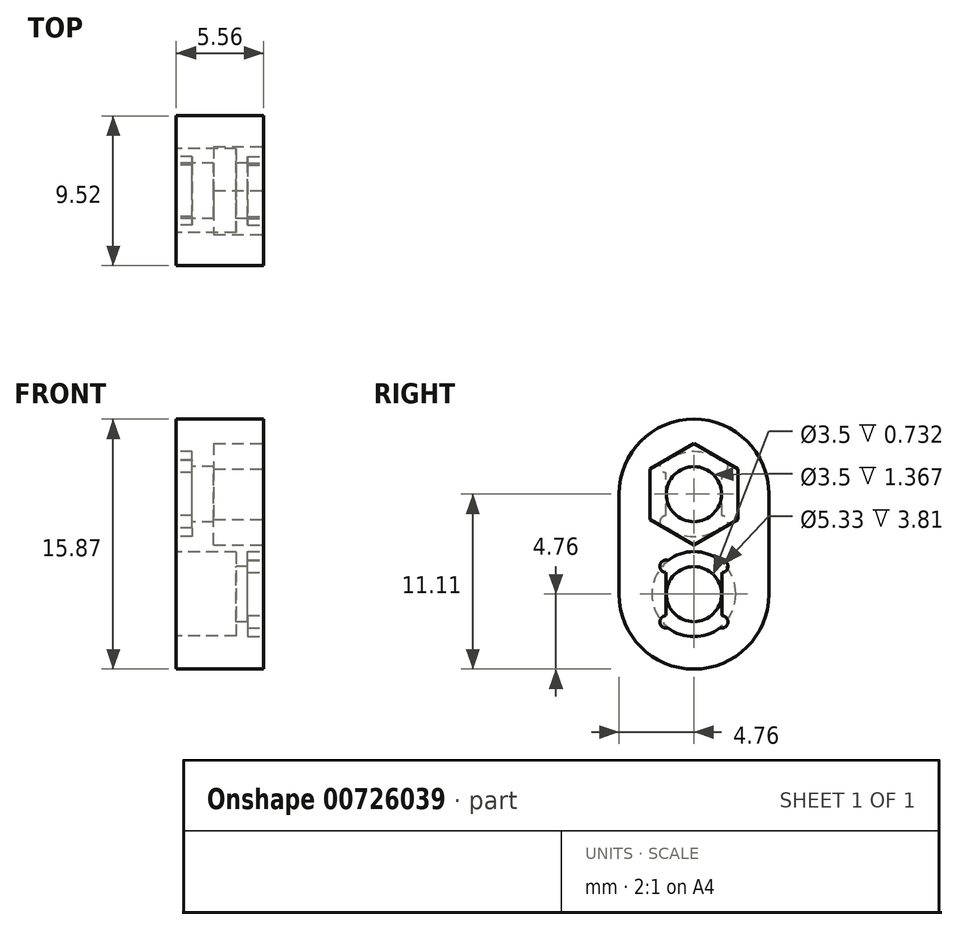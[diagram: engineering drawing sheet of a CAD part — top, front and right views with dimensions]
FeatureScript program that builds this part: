
annotation { "Feature Type Name" : "Feature", "Feature Type Description" : "" }
export const myFeature = defineFeature(function(context is Context, id is Id, definition is map)
    precondition{}
    {
        {
            var Q0;
            Q0=qCreatedBy(makeId("Right.planeOp"),FACE);
            var sketch = newSketch(context, id + "F0", { "sketchPlane" : qUnion([Q0])});
            skCircle(sketch, "E0", {"center": v(0, 0) * mm, "radius": 4.76 * mm});
            skCircle(sketch, "E1", {"center": v(0, 0) * mm, "radius": 1.75 * mm});
            skCircle(sketch, "E2", {"center": v(0, -6.35) * mm, "radius": 4.76 * mm});
            skCircle(sketch, "E3", {"center": v(0, -6.35) * mm, "radius": 1.75 * mm});
            skLineSegment(sketch, "E4", {"start": v(-4.76, 0) * mm, "end": v(-4.76, -6.35) * mm});
            skLineSegment(sketch, "E5", {"start": v(4.76, 0) * mm, "end": v(4.76, -6.35) * mm});
            skSolve(sketch);
        }
        {
            var Q0;
            Q0=makeQuery(id+"F0.imprint","IMPRINT",FACE,{"disambiguationData":[TD([[makeQuery(id+"F0.imprint","IMPRINT",EDGE,{"derivedFrom":sQuery(id+"F0.wireOp",EDGE,"E1")}),-1.0]])]});
            var Q1;
            {var subQ0=sQuery(id+"F0.wireOp",EDGE,"E5");Q1=makeQuery(id+"F0.imprint","IMPRINT",FACE,{"disambiguationData":[TD([[makeQuery(id+"F0.imprint","IMPRINT",EDGE,{"derivedFrom":subQ0}),-1.0]])]});}
            var Q2;
            {var subQ0=sQuery(id+"F0.wireOp",EDGE,"E2");var subQ1=sQuery(id+"F0.wireOp",EDGE,"E0");var subQ2=makeQuery(id+"F0.imprint","INTERSECT",VERTEX,{"disambiguationData":[OD(0.0)],"derivedFrom":[subQ1,subQ0]});Q2=makeQuery(id+"F0.imprint","IMPRINT",FACE,{"disambiguationData":[TD([[makeQuery(id+"F0.imprint","IMPRINT",EDGE,{"disambiguationData":[TD([[subQ2,-1.0]])],"derivedFrom":subQ1}),1.0]])]});}
            var Q3;
            Q3=makeQuery(id+"F0.imprint","IMPRINT",FACE,{"disambiguationData":[TD([[makeQuery(id+"F0.imprint","IMPRINT",EDGE,{"derivedFrom":sQuery(id+"F0.wireOp",EDGE,"E3")}),-1.0]])]});
            var Q4;
            {var subQ0=sQuery(id+"F0.wireOp",EDGE,"E4");Q4=makeQuery(id+"F0.imprint","IMPRINT",FACE,{"disambiguationData":[TD([[makeQuery(id+"F0.imprint","IMPRINT",EDGE,{"derivedFrom":subQ0}),1.0]])]});}
            extrude(context, id + "F1", {"entities" : qUnion([Q0, Q1, Q2, Q3, Q4]), "depth" : 5.56 * mm, "offsetDistance" : 25.4 * mm});
        }
        {
            var Q0;
            Q0=makeQuery(id+"F1.opExtrude","CAP_FACE",FACE,{"disambiguationData":[OSD([sQuery(id+"F0.wireOp",EDGE,"E0"),sQuery(id+"F0.wireOp",EDGE,"E1"),sQuery(id+"F0.wireOp",EDGE,"E2"),sQuery(id+"F0.wireOp",EDGE,"E3"),sQuery(id+"F0.wireOp",EDGE,"E4"),sQuery(id+"F0.wireOp",EDGE,"E5")])],"isStart":false});
            var sketch = newSketch(context, id + "F2", { "sketchPlane" : qUnion([Q0])});
            skLineSegment(sketch, "E6.bottom", {"start": v(-1.77, -8.12) * mm, "end": v(1.77, -8.12) * mm});
            skLineSegment(sketch, "E6.top", {"start": v(-1.77, -4.58) * mm, "end": v(1.77, -4.58) * mm});
            skLineSegment(sketch, "E6.left", {"start": v(-1.77, -8.12) * mm, "end": v(-1.77, -4.58) * mm});
            skLineSegment(sketch, "E6.right", {"start": v(1.77, -8.12) * mm, "end": v(1.77, -4.58) * mm});
            skPoint(sketch, "E6.middle", {"position": v(0, -6.35) * mm});
            skCircle(sketch, "E7", {"center": v(1.77, -4.58) * mm, "radius": 0.4 * mm});
            skCircle(sketch, "E8", {"center": v(-1.77, -4.58) * mm, "radius": 0.4 * mm});
            skCircle(sketch, "E9", {"center": v(-1.77, -8.12) * mm, "radius": 0.4 * mm});
            skCircle(sketch, "E10", {"center": v(1.77, -8.12) * mm, "radius": 0.4 * mm});
            skCircle(sketch, "E11.cCircle", {"center": v(0, 0) * mm, "radius": 3.23 * mm, "construction": true});
            skLineSegment(sketch, "E11.0", {"start": v(0, -3.23) * mm, "end": v(-2.8, -1.61) * mm});
            skLineSegment(sketch, "E11.1", {"start": v(-2.8, -1.61) * mm, "end": v(-2.8, 1.61) * mm});
            skLineSegment(sketch, "E11.2", {"start": v(-2.8, 1.61) * mm, "end": v(0, 3.23) * mm});
            skLineSegment(sketch, "E11.3", {"start": v(0, 3.23) * mm, "end": v(2.8, 1.61) * mm});
            skLineSegment(sketch, "E11.4", {"start": v(2.8, 1.61) * mm, "end": v(2.8, -1.61) * mm});
            skLineSegment(sketch, "E11.5", {"start": v(2.8, -1.61) * mm, "end": v(0, -3.23) * mm});
            skCircle(sketch, "E12", {"center": v(0, -6.35) * mm, "radius": 2.7 * mm});
            skSolve(sketch);
        }
        {
            var Q0;
            {var subQ0=sQuery(id+"F2.wireOp",EDGE,"E6.right");var subQ1=sQuery(id+"F2.wireOp",EDGE,"E6.top");var subQ2=makeQuery(id+"F2.imprint","INTERSECT",VERTEX,{"derivedFrom":[subQ1,subQ0]});Q0=makeQuery(id+"F2.imprint","IMPRINT",FACE,{"disambiguationData":[TD([[makeQuery(id+"F2.imprint","IMPRINT",EDGE,{"disambiguationData":[TD([[subQ2,1.0]])],"derivedFrom":subQ1}),-1.0]])]});}
            var Q1;
            {var subQ0=sQuery(id+"F2.wireOp",EDGE,"E6.right");var subQ1=sQuery(id+"F2.wireOp",EDGE,"E6.top");var subQ2=makeQuery(id+"F2.imprint","INTERSECT",VERTEX,{"derivedFrom":[subQ1,subQ0]});Q1=makeQuery(id+"F2.imprint","IMPRINT",FACE,{"disambiguationData":[TD([[makeQuery(id+"F2.imprint","IMPRINT",EDGE,{"disambiguationData":[TD([[subQ2,1.0]])],"derivedFrom":subQ1}),1.0]])]});}
            var Q2;
            {var subQ0=sQuery(id+"F2.wireOp",EDGE,"E6.right");var subQ1=sQuery(id+"F2.wireOp",EDGE,"E6.bottom");var subQ2=makeQuery(id+"F2.imprint","INTERSECT",VERTEX,{"derivedFrom":[subQ1,subQ0]});Q2=makeQuery(id+"F2.imprint","IMPRINT",FACE,{"disambiguationData":[TD([[makeQuery(id+"F2.imprint","IMPRINT",EDGE,{"disambiguationData":[TD([[subQ2,1.0]])],"derivedFrom":subQ1}),1.0]])]});}
            var Q3;
            {var subQ0=sQuery(id+"F2.wireOp",EDGE,"E6.right");var subQ1=sQuery(id+"F2.wireOp",EDGE,"E6.bottom");var subQ2=makeQuery(id+"F2.imprint","INTERSECT",VERTEX,{"derivedFrom":[subQ1,subQ0]});Q3=makeQuery(id+"F2.imprint","IMPRINT",FACE,{"disambiguationData":[TD([[makeQuery(id+"F2.imprint","IMPRINT",EDGE,{"disambiguationData":[TD([[subQ2,1.0]])],"derivedFrom":subQ1}),-1.0]])]});}
            var Q4;
            {var subQ0=sQuery(id+"F2.wireOp",EDGE,"E6.left");var subQ1=sQuery(id+"F2.wireOp",EDGE,"E6.bottom");var subQ2=makeQuery(id+"F2.imprint","INTERSECT",VERTEX,{"derivedFrom":[subQ1,subQ0]});Q4=makeQuery(id+"F2.imprint","IMPRINT",FACE,{"disambiguationData":[TD([[makeQuery(id+"F2.imprint","IMPRINT",EDGE,{"disambiguationData":[TD([[subQ2,-1.0]])],"derivedFrom":subQ1}),-1.0]])]});}
            var Q5;
            {var subQ0=sQuery(id+"F2.wireOp",EDGE,"E6.left");var subQ1=sQuery(id+"F2.wireOp",EDGE,"E6.bottom");var subQ2=makeQuery(id+"F2.imprint","INTERSECT",VERTEX,{"derivedFrom":[subQ1,subQ0]});Q5=makeQuery(id+"F2.imprint","IMPRINT",FACE,{"disambiguationData":[TD([[makeQuery(id+"F2.imprint","IMPRINT",EDGE,{"disambiguationData":[TD([[subQ2,-1.0]])],"derivedFrom":subQ1}),1.0]])]});}
            var Q6;
            {var subQ0=sQuery(id+"F2.wireOp",EDGE,"E6.left");var subQ1=sQuery(id+"F2.wireOp",EDGE,"E6.top");var subQ2=makeQuery(id+"F2.imprint","INTERSECT",VERTEX,{"derivedFrom":[subQ1,subQ0]});Q6=makeQuery(id+"F2.imprint","IMPRINT",FACE,{"disambiguationData":[TD([[makeQuery(id+"F2.imprint","IMPRINT",EDGE,{"disambiguationData":[TD([[subQ2,-1.0]])],"derivedFrom":subQ1}),-1.0]])]});}
            var Q7;
            {var subQ0=sQuery(id+"F2.wireOp",EDGE,"E6.left");var subQ1=sQuery(id+"F2.wireOp",EDGE,"E6.top");var subQ2=makeQuery(id+"F2.imprint","INTERSECT",VERTEX,{"derivedFrom":[subQ1,subQ0]});Q7=makeQuery(id+"F2.imprint","IMPRINT",FACE,{"disambiguationData":[TD([[makeQuery(id+"F2.imprint","IMPRINT",EDGE,{"disambiguationData":[TD([[subQ2,-1.0]])],"derivedFrom":subQ1}),1.0]])]});}
            var Q8;
            {var subQ1=sQuery(id+"F2.wireOp",EDGE,"E6.top");var subQ7=sQuery(id+"F2.wireOp",EDGE,"E8");var subQ11=makeQuery(id+"F2.imprint","INTERSECT",VERTEX,{"derivedFrom":[subQ1,subQ7]});Q8=makeQuery(id+"F2.imprint","IMPRINT",FACE,{"disambiguationData":[TD([[makeQuery(id+"F2.imprint","IMPRINT",EDGE,{"disambiguationData":[TD([[subQ11,-1.0]])],"derivedFrom":subQ1}),-1.0]])]});}
            var Q9;
            {var subQ0=sQuery(id+"F2.wireOp",EDGE,"E9");var subQ1=sQuery(id+"F2.wireOp",EDGE,"E6.bottom");var subQ2=makeQuery(id+"F2.imprint","INTERSECT",VERTEX,{"derivedFrom":[subQ1,subQ0]});Q9=makeQuery(id+"F2.imprint","IMPRINT",FACE,{"disambiguationData":[TD([[makeQuery(id+"F2.imprint","IMPRINT",EDGE,{"disambiguationData":[TD([[subQ2,-1.0]])],"derivedFrom":subQ1}),1.0]])]});}
            var Q10;
            {var subQ0=sQuery(id+"F2.wireOp",EDGE,"E12");var subQ1=sQuery(id+"F2.wireOp",EDGE,"E6.top");var subQ10=makeQuery(id+"F2.imprint","INTERSECT",VERTEX,{"disambiguationData":[OD(0.0)],"derivedFrom":[subQ1,subQ0]});Q10=makeQuery(id+"F2.imprint","IMPRINT",FACE,{"disambiguationData":[TD([[makeQuery(id+"F2.imprint","IMPRINT",EDGE,{"disambiguationData":[TD([[subQ10,-1.0]])],"derivedFrom":subQ1}),-1.0]])]});}
            var Q11;
            {var subQ0=sQuery(id+"F2.wireOp",EDGE,"E12");var subQ1=sQuery(id+"F2.wireOp",EDGE,"E6.top");var subQ2=makeQuery(id+"F2.imprint","INTERSECT",VERTEX,{"disambiguationData":[OD(1.0)],"derivedFrom":[subQ1,subQ0]});Q11=makeQuery(id+"F2.imprint","IMPRINT",FACE,{"disambiguationData":[TD([[makeQuery(id+"F2.imprint","IMPRINT",EDGE,{"disambiguationData":[TD([[subQ2,-1.0]])],"derivedFrom":subQ1}),-1.0]])]});}
            var Q12;
            {var subQ0=sQuery(id+"F2.wireOp",EDGE,"E12");var subQ1=sQuery(id+"F2.wireOp",EDGE,"E6.top");var subQ2=makeQuery(id+"F2.imprint","INTERSECT",VERTEX,{"disambiguationData":[OD(0.0)],"derivedFrom":[subQ1,subQ0]});Q12=makeQuery(id+"F2.imprint","IMPRINT",FACE,{"disambiguationData":[TD([[makeQuery(id+"F2.imprint","IMPRINT",EDGE,{"disambiguationData":[TD([[subQ2,-1.0]])],"derivedFrom":subQ1}),1.0]])]});}
            var Q13;
            {var subQ0=sQuery(id+"F2.wireOp",EDGE,"E12");var subQ7=sQuery(id+"F2.wireOp",EDGE,"E6.bottom");var subQ8=makeQuery(id+"F2.imprint","INTERSECT",VERTEX,{"disambiguationData":[OD(0.0)],"derivedFrom":[subQ7,subQ0]});Q13=makeQuery(id+"F2.imprint","IMPRINT",FACE,{"disambiguationData":[TD([[makeQuery(id+"F2.imprint","IMPRINT",EDGE,{"disambiguationData":[TD([[subQ8,-1.0]])],"derivedFrom":subQ7}),1.0]])]});}
            var Q14;
            {var subQ0=sQuery(id+"F2.wireOp",EDGE,"E12");var subQ1=sQuery(id+"F2.wireOp",EDGE,"E6.bottom");var subQ2=makeQuery(id+"F2.imprint","INTERSECT",VERTEX,{"disambiguationData":[OD(1.0)],"derivedFrom":[subQ1,subQ0]});Q14=makeQuery(id+"F2.imprint","IMPRINT",FACE,{"disambiguationData":[TD([[makeQuery(id+"F2.imprint","IMPRINT",EDGE,{"disambiguationData":[TD([[subQ2,-1.0]])],"derivedFrom":subQ1}),1.0]])]});}
            var Q15;
            {var subQ0=sQuery(id+"F2.wireOp",EDGE,"E12");var subQ1=sQuery(id+"F2.wireOp",EDGE,"E6.bottom");var subQ2=makeQuery(id+"F2.imprint","INTERSECT",VERTEX,{"disambiguationData":[OD(0.0)],"derivedFrom":[subQ1,subQ0]});Q15=makeQuery(id+"F2.imprint","IMPRINT",FACE,{"disambiguationData":[TD([[makeQuery(id+"F2.imprint","IMPRINT",EDGE,{"disambiguationData":[TD([[subQ2,-1.0]])],"derivedFrom":subQ1}),-1.0]])]});}
            var Q16;
            {var subQ0=sQuery(id+"F2.wireOp",EDGE,"E12");var subQ1=sQuery(id+"F2.wireOp",EDGE,"E8");var subQ2=makeQuery(id+"F2.imprint","INTERSECT",VERTEX,{"disambiguationData":[OD(0.0)],"derivedFrom":[subQ1,subQ0]});Q16=makeQuery(id+"F2.imprint","IMPRINT",FACE,{"disambiguationData":[TD([[makeQuery(id+"F2.imprint","IMPRINT",EDGE,{"disambiguationData":[TD([[subQ2,-1.0]])],"derivedFrom":subQ1}),1.0]])]});}
            var Q17;
            {var subQ0=sQuery(id+"F2.wireOp",EDGE,"E12");var subQ1=sQuery(id+"F2.wireOp",EDGE,"E7");var subQ2=makeQuery(id+"F2.imprint","INTERSECT",VERTEX,{"disambiguationData":[OD(0.0)],"derivedFrom":[subQ1,subQ0]});Q17=makeQuery(id+"F2.imprint","IMPRINT",FACE,{"disambiguationData":[TD([[makeQuery(id+"F2.imprint","IMPRINT",EDGE,{"disambiguationData":[TD([[subQ2,1.0]])],"derivedFrom":subQ1}),1.0]])]});}
            var Q18;
            {var subQ0=sQuery(id+"F2.wireOp",EDGE,"E12");var subQ1=sQuery(id+"F2.wireOp",EDGE,"E10");var subQ2=makeQuery(id+"F2.imprint","INTERSECT",VERTEX,{"disambiguationData":[OD(0.0)],"derivedFrom":[subQ1,subQ0]});Q18=makeQuery(id+"F2.imprint","IMPRINT",FACE,{"disambiguationData":[TD([[makeQuery(id+"F2.imprint","IMPRINT",EDGE,{"disambiguationData":[TD([[subQ2,1.0]])],"derivedFrom":subQ1}),1.0]])]});}
            var Q19;
            {var subQ0=sQuery(id+"F2.wireOp",EDGE,"E12");var subQ1=sQuery(id+"F2.wireOp",EDGE,"E9");var subQ2=makeQuery(id+"F2.imprint","INTERSECT",VERTEX,{"disambiguationData":[OD(0.0)],"derivedFrom":[subQ1,subQ0]});Q19=makeQuery(id+"F2.imprint","IMPRINT",FACE,{"disambiguationData":[TD([[makeQuery(id+"F2.imprint","IMPRINT",EDGE,{"disambiguationData":[TD([[subQ2,-1.0]])],"derivedFrom":subQ1}),1.0]])]});}
            var Q20;
            {var subQ0=sQuery(id+"F2.wireOp",EDGE,"E8");var subQ1=sQuery(id+"F2.wireOp",EDGE,"E6.top");var subQ2=makeQuery(id+"F2.imprint","INTERSECT",VERTEX,{"derivedFrom":[subQ1,subQ0]});Q20=makeQuery(id+"F2.imprint","IMPRINT",FACE,{"disambiguationData":[TD([[makeQuery(id+"F2.imprint","IMPRINT",EDGE,{"disambiguationData":[TD([[subQ2,-1.0]])],"derivedFrom":subQ1}),1.0]])]});}
            var Q21;
            {var subQ0=sQuery(id+"F2.wireOp",EDGE,"E9");var subQ1=sQuery(id+"F2.wireOp",EDGE,"E6.bottom");var subQ2=makeQuery(id+"F2.imprint","INTERSECT",VERTEX,{"derivedFrom":[subQ1,subQ0]});Q21=makeQuery(id+"F2.imprint","IMPRINT",FACE,{"disambiguationData":[TD([[makeQuery(id+"F2.imprint","IMPRINT",EDGE,{"disambiguationData":[TD([[subQ2,-1.0]])],"derivedFrom":subQ1}),-1.0]])]});}
            extrude(context, id + "F3", {"entities" : qUnion([Q0, Q1, Q2, Q3, Q4, Q5, Q6, Q7, Q8, Q9, Q10, Q11, Q12, Q13, Q14, Q15, Q16, Q17, Q18, Q19, Q20, Q21]), "operationType" : NewBodyOperationType.REMOVE, "oppositeDirection" : true, "depth" : 1.02 * mm, "offsetDistance" : 25.4 * mm});
        }
        {
            var Q0;
            Q0=makeQuery(id+"F1.opExtrude","CAP_FACE",FACE,{"disambiguationData":[OSD([sQuery(id+"F0.wireOp",EDGE,"E0"),sQuery(id+"F0.wireOp",EDGE,"E1"),sQuery(id+"F0.wireOp",EDGE,"E2"),sQuery(id+"F0.wireOp",EDGE,"E3"),sQuery(id+"F0.wireOp",EDGE,"E4"),sQuery(id+"F0.wireOp",EDGE,"E5")])],"isStart":true});
            var sketch = newSketch(context, id + "F4", { "sketchPlane" : qUnion([Q0])});
            skLineSegment(sketch, "E13.bottom", {"start": v(-1.77, -1.77) * mm, "end": v(1.77, -1.77) * mm});
            skLineSegment(sketch, "E13.top", {"start": v(-1.77, 1.77) * mm, "end": v(1.77, 1.77) * mm});
            skLineSegment(sketch, "E13.left", {"start": v(-1.77, -1.77) * mm, "end": v(-1.77, 1.77) * mm});
            skLineSegment(sketch, "E13.right", {"start": v(1.77, -1.77) * mm, "end": v(1.77, 1.77) * mm});
            skPoint(sketch, "E13.middle", {"position": v(0, 0) * mm});
            skCircle(sketch, "E14", {"center": v(1.77, 1.77) * mm, "radius": 0.4 * mm});
            skCircle(sketch, "E15", {"center": v(-1.77, 1.77) * mm, "radius": 0.4 * mm});
            skCircle(sketch, "E16", {"center": v(-1.77, -1.77) * mm, "radius": 0.4 * mm});
            skCircle(sketch, "E17", {"center": v(1.77, -1.77) * mm, "radius": 0.4 * mm});
            skCircle(sketch, "E18.cCircle", {"center": v(0, -6.35) * mm, "radius": 3.23 * mm, "construction": true});
            skLineSegment(sketch, "E18.0", {"start": v(0, -9.58) * mm, "end": v(-2.8, -7.96) * mm});
            skLineSegment(sketch, "E18.1", {"start": v(-2.8, -7.96) * mm, "end": v(-2.8, -4.74) * mm});
            skLineSegment(sketch, "E18.2", {"start": v(-2.8, -4.74) * mm, "end": v(0, -3.12) * mm});
            skLineSegment(sketch, "E18.3", {"start": v(0, -3.12) * mm, "end": v(2.8, -4.74) * mm});
            skLineSegment(sketch, "E18.4", {"start": v(2.8, -4.74) * mm, "end": v(2.8, -7.96) * mm});
            skLineSegment(sketch, "E18.5", {"start": v(2.8, -7.96) * mm, "end": v(0, -9.58) * mm});
            skCircle(sketch, "E19", {"center": v(0, 0) * mm, "radius": 2.7 * mm});
            skSolve(sketch);
        }
        {
            var Q0;
            {var subQ0=sQuery(id+"F4.wireOp",EDGE,"E13.right");var subQ1=sQuery(id+"F4.wireOp",EDGE,"E13.bottom");var subQ2=makeQuery(id+"F4.imprint","INTERSECT",VERTEX,{"derivedFrom":[subQ1,subQ0]});Q0=makeQuery(id+"F4.imprint","IMPRINT",FACE,{"disambiguationData":[TD([[makeQuery(id+"F4.imprint","IMPRINT",EDGE,{"disambiguationData":[TD([[subQ2,1.0]])],"derivedFrom":subQ1}),1.0]])]});}
            var Q1;
            {var subQ0=sQuery(id+"F4.wireOp",EDGE,"E13.right");var subQ1=sQuery(id+"F4.wireOp",EDGE,"E13.bottom");var subQ2=makeQuery(id+"F4.imprint","INTERSECT",VERTEX,{"derivedFrom":[subQ1,subQ0]});Q1=makeQuery(id+"F4.imprint","IMPRINT",FACE,{"disambiguationData":[TD([[makeQuery(id+"F4.imprint","IMPRINT",EDGE,{"disambiguationData":[TD([[subQ2,1.0]])],"derivedFrom":subQ1}),-1.0]])]});}
            var Q2;
            {var subQ0=sQuery(id+"F4.wireOp",EDGE,"E13.left");var subQ1=sQuery(id+"F4.wireOp",EDGE,"E13.bottom");var subQ2=makeQuery(id+"F4.imprint","INTERSECT",VERTEX,{"derivedFrom":[subQ1,subQ0]});Q2=makeQuery(id+"F4.imprint","IMPRINT",FACE,{"disambiguationData":[TD([[makeQuery(id+"F4.imprint","IMPRINT",EDGE,{"disambiguationData":[TD([[subQ2,-1.0]])],"derivedFrom":subQ1}),1.0]])]});}
            var Q3;
            {var subQ0=sQuery(id+"F4.wireOp",EDGE,"E13.left");var subQ1=sQuery(id+"F4.wireOp",EDGE,"E13.bottom");var subQ2=makeQuery(id+"F4.imprint","INTERSECT",VERTEX,{"derivedFrom":[subQ1,subQ0]});Q3=makeQuery(id+"F4.imprint","IMPRINT",FACE,{"disambiguationData":[TD([[makeQuery(id+"F4.imprint","IMPRINT",EDGE,{"disambiguationData":[TD([[subQ2,-1.0]])],"derivedFrom":subQ1}),-1.0]])]});}
            var Q4;
            {var subQ0=sQuery(id+"F4.wireOp",EDGE,"E13.left");var subQ1=sQuery(id+"F4.wireOp",EDGE,"E13.top");var subQ2=makeQuery(id+"F4.imprint","INTERSECT",VERTEX,{"derivedFrom":[subQ1,subQ0]});Q4=makeQuery(id+"F4.imprint","IMPRINT",FACE,{"disambiguationData":[TD([[makeQuery(id+"F4.imprint","IMPRINT",EDGE,{"disambiguationData":[TD([[subQ2,-1.0]])],"derivedFrom":subQ1}),-1.0]])]});}
            var Q5;
            {var subQ0=sQuery(id+"F4.wireOp",EDGE,"E13.left");var subQ1=sQuery(id+"F4.wireOp",EDGE,"E13.top");var subQ2=makeQuery(id+"F4.imprint","INTERSECT",VERTEX,{"derivedFrom":[subQ1,subQ0]});Q5=makeQuery(id+"F4.imprint","IMPRINT",FACE,{"disambiguationData":[TD([[makeQuery(id+"F4.imprint","IMPRINT",EDGE,{"disambiguationData":[TD([[subQ2,-1.0]])],"derivedFrom":subQ1}),1.0]])]});}
            var Q6;
            {var subQ0=sQuery(id+"F4.wireOp",EDGE,"E13.right");var subQ1=sQuery(id+"F4.wireOp",EDGE,"E13.top");var subQ2=makeQuery(id+"F4.imprint","INTERSECT",VERTEX,{"derivedFrom":[subQ1,subQ0]});Q6=makeQuery(id+"F4.imprint","IMPRINT",FACE,{"disambiguationData":[TD([[makeQuery(id+"F4.imprint","IMPRINT",EDGE,{"disambiguationData":[TD([[subQ2,1.0]])],"derivedFrom":subQ1}),-1.0]])]});}
            var Q7;
            {var subQ0=sQuery(id+"F4.wireOp",EDGE,"E13.right");var subQ1=sQuery(id+"F4.wireOp",EDGE,"E13.top");var subQ2=makeQuery(id+"F4.imprint","INTERSECT",VERTEX,{"derivedFrom":[subQ1,subQ0]});Q7=makeQuery(id+"F4.imprint","IMPRINT",FACE,{"disambiguationData":[TD([[makeQuery(id+"F4.imprint","IMPRINT",EDGE,{"disambiguationData":[TD([[subQ2,1.0]])],"derivedFrom":subQ1}),1.0]])]});}
            var Q8;
            {var subQ0=sQuery(id+"F4.wireOp",EDGE,"E13.left");var subQ1=makeQuery(id+"F1.opExtrude","CAP_EDGE",EDGE,{"disambiguationData":[OSD([sQuery(id+"F0.wireOp",EDGE,"E1")])],"isStart":true});var subQ2=makeQuery(id+"F4.imprint","INTERSECT",VERTEX,{"disambiguationData":[OD(0.0)],"derivedFrom":[subQ1,subQ0]});Q8=makeQuery(id+"F4.imprint","IMPRINT",FACE,{"disambiguationData":[TD([[makeQuery(id+"F4.imprint","IMPRINT",EDGE,{"disambiguationData":[TD([[subQ2,-1.0]])],"derivedFrom":subQ0}),-1.0]])]});}
            var Q9;
            {var subQ0=sQuery(id+"F4.wireOp",EDGE,"E16");var subQ1=sQuery(id+"F4.wireOp",EDGE,"E13.bottom");var subQ2=makeQuery(id+"F4.imprint","INTERSECT",VERTEX,{"derivedFrom":[subQ1,subQ0]});Q9=makeQuery(id+"F4.imprint","IMPRINT",FACE,{"disambiguationData":[TD([[makeQuery(id+"F4.imprint","IMPRINT",EDGE,{"disambiguationData":[TD([[subQ2,-1.0]])],"derivedFrom":subQ1}),1.0]])]});}
            var Q10;
            {var subQ1=sQuery(id+"F4.wireOp",EDGE,"E13.top");var subQ7=sQuery(id+"F4.wireOp",EDGE,"E15");var subQ11=makeQuery(id+"F4.imprint","INTERSECT",VERTEX,{"derivedFrom":[subQ1,subQ7]});Q10=makeQuery(id+"F4.imprint","IMPRINT",FACE,{"disambiguationData":[TD([[makeQuery(id+"F4.imprint","IMPRINT",EDGE,{"disambiguationData":[TD([[subQ11,-1.0]])],"derivedFrom":subQ1}),-1.0]])]});}
            var Q11;
            {var subQ0=sQuery(id+"F4.wireOp",EDGE,"E19");var subQ1=sQuery(id+"F4.wireOp",EDGE,"E13.top");var subQ10=makeQuery(id+"F4.imprint","INTERSECT",VERTEX,{"disambiguationData":[OD(0.0)],"derivedFrom":[subQ1,subQ0]});Q11=makeQuery(id+"F4.imprint","IMPRINT",FACE,{"disambiguationData":[TD([[makeQuery(id+"F4.imprint","IMPRINT",EDGE,{"disambiguationData":[TD([[subQ10,-1.0]])],"derivedFrom":subQ1}),-1.0]])]});}
            var Q12;
            {var subQ0=sQuery(id+"F4.wireOp",EDGE,"E19");var subQ1=sQuery(id+"F4.wireOp",EDGE,"E13.top");var subQ2=makeQuery(id+"F4.imprint","INTERSECT",VERTEX,{"disambiguationData":[OD(1.0)],"derivedFrom":[subQ1,subQ0]});Q12=makeQuery(id+"F4.imprint","IMPRINT",FACE,{"disambiguationData":[TD([[makeQuery(id+"F4.imprint","IMPRINT",EDGE,{"disambiguationData":[TD([[subQ2,-1.0]])],"derivedFrom":subQ1}),-1.0]])]});}
            var Q13;
            {var subQ0=sQuery(id+"F4.wireOp",EDGE,"E19");var subQ7=sQuery(id+"F4.wireOp",EDGE,"E13.bottom");var subQ8=makeQuery(id+"F4.imprint","INTERSECT",VERTEX,{"disambiguationData":[OD(0.0)],"derivedFrom":[subQ7,subQ0]});Q13=makeQuery(id+"F4.imprint","IMPRINT",FACE,{"disambiguationData":[TD([[makeQuery(id+"F4.imprint","IMPRINT",EDGE,{"disambiguationData":[TD([[subQ8,-1.0]])],"derivedFrom":subQ7}),1.0]])]});}
            var Q14;
            {var subQ0=sQuery(id+"F4.wireOp",EDGE,"E19");var subQ1=sQuery(id+"F4.wireOp",EDGE,"E13.bottom");var subQ2=makeQuery(id+"F4.imprint","INTERSECT",VERTEX,{"disambiguationData":[OD(1.0)],"derivedFrom":[subQ1,subQ0]});Q14=makeQuery(id+"F4.imprint","IMPRINT",FACE,{"disambiguationData":[TD([[makeQuery(id+"F4.imprint","IMPRINT",EDGE,{"disambiguationData":[TD([[subQ2,-1.0]])],"derivedFrom":subQ1}),1.0]])]});}
            var Q15;
            {var subQ0=sQuery(id+"F4.wireOp",EDGE,"E19");var subQ1=sQuery(id+"F4.wireOp",EDGE,"E13.top");var subQ2=makeQuery(id+"F4.imprint","INTERSECT",VERTEX,{"disambiguationData":[OD(0.0)],"derivedFrom":[subQ1,subQ0]});Q15=makeQuery(id+"F4.imprint","IMPRINT",FACE,{"disambiguationData":[TD([[makeQuery(id+"F4.imprint","IMPRINT",EDGE,{"disambiguationData":[TD([[subQ2,-1.0]])],"derivedFrom":subQ1}),1.0]])]});}
            var Q16;
            {var subQ0=sQuery(id+"F4.wireOp",EDGE,"E19");var subQ1=sQuery(id+"F4.wireOp",EDGE,"E13.bottom");var subQ2=makeQuery(id+"F4.imprint","INTERSECT",VERTEX,{"disambiguationData":[OD(0.0)],"derivedFrom":[subQ1,subQ0]});Q16=makeQuery(id+"F4.imprint","IMPRINT",FACE,{"disambiguationData":[TD([[makeQuery(id+"F4.imprint","IMPRINT",EDGE,{"disambiguationData":[TD([[subQ2,-1.0]])],"derivedFrom":subQ1}),-1.0]])]});}
            var Q17;
            {var subQ0=sQuery(id+"F4.wireOp",EDGE,"E19");var subQ1=sQuery(id+"F4.wireOp",EDGE,"E15");var subQ2=makeQuery(id+"F4.imprint","INTERSECT",VERTEX,{"disambiguationData":[OD(0.0)],"derivedFrom":[subQ1,subQ0]});Q17=makeQuery(id+"F4.imprint","IMPRINT",FACE,{"disambiguationData":[TD([[makeQuery(id+"F4.imprint","IMPRINT",EDGE,{"disambiguationData":[TD([[subQ2,-1.0]])],"derivedFrom":subQ1}),1.0]])]});}
            var Q18;
            {var subQ0=sQuery(id+"F4.wireOp",EDGE,"E19");var subQ1=sQuery(id+"F4.wireOp",EDGE,"E14");var subQ2=makeQuery(id+"F4.imprint","INTERSECT",VERTEX,{"disambiguationData":[OD(0.0)],"derivedFrom":[subQ1,subQ0]});Q18=makeQuery(id+"F4.imprint","IMPRINT",FACE,{"disambiguationData":[TD([[makeQuery(id+"F4.imprint","IMPRINT",EDGE,{"disambiguationData":[TD([[subQ2,1.0]])],"derivedFrom":subQ1}),1.0]])]});}
            var Q19;
            {var subQ0=sQuery(id+"F4.wireOp",EDGE,"E19");var subQ1=sQuery(id+"F4.wireOp",EDGE,"E17");var subQ2=makeQuery(id+"F4.imprint","INTERSECT",VERTEX,{"disambiguationData":[OD(0.0)],"derivedFrom":[subQ1,subQ0]});Q19=makeQuery(id+"F4.imprint","IMPRINT",FACE,{"disambiguationData":[TD([[makeQuery(id+"F4.imprint","IMPRINT",EDGE,{"disambiguationData":[TD([[subQ2,1.0]])],"derivedFrom":subQ1}),1.0]])]});}
            var Q20;
            {var subQ0=sQuery(id+"F4.wireOp",EDGE,"E19");var subQ1=sQuery(id+"F4.wireOp",EDGE,"E16");var subQ2=makeQuery(id+"F4.imprint","INTERSECT",VERTEX,{"disambiguationData":[OD(0.0)],"derivedFrom":[subQ1,subQ0]});Q20=makeQuery(id+"F4.imprint","IMPRINT",FACE,{"disambiguationData":[TD([[makeQuery(id+"F4.imprint","IMPRINT",EDGE,{"disambiguationData":[TD([[subQ2,-1.0]])],"derivedFrom":subQ1}),1.0]])]});}
            var Q21;
            {var subQ0=sQuery(id+"F4.wireOp",EDGE,"E16");var subQ1=sQuery(id+"F4.wireOp",EDGE,"E13.bottom");var subQ2=makeQuery(id+"F4.imprint","INTERSECT",VERTEX,{"derivedFrom":[subQ1,subQ0]});Q21=makeQuery(id+"F4.imprint","IMPRINT",FACE,{"disambiguationData":[TD([[makeQuery(id+"F4.imprint","IMPRINT",EDGE,{"disambiguationData":[TD([[subQ2,-1.0]])],"derivedFrom":subQ1}),-1.0]])]});}
            var Q22;
            {var subQ0=sQuery(id+"F4.wireOp",EDGE,"E15");var subQ1=sQuery(id+"F4.wireOp",EDGE,"E13.top");var subQ2=makeQuery(id+"F4.imprint","INTERSECT",VERTEX,{"derivedFrom":[subQ1,subQ0]});Q22=makeQuery(id+"F4.imprint","IMPRINT",FACE,{"disambiguationData":[TD([[makeQuery(id+"F4.imprint","IMPRINT",EDGE,{"disambiguationData":[TD([[subQ2,-1.0]])],"derivedFrom":subQ1}),1.0]])]});}
            extrude(context, id + "F5", {"entities" : qUnion([Q0, Q1, Q2, Q3, Q4, Q5, Q6, Q7, Q8, Q9, Q10, Q11, Q12, Q13, Q14, Q15, Q16, Q17, Q18, Q19, Q20, Q21, Q22]), "operationType" : NewBodyOperationType.REMOVE, "oppositeDirection" : true, "depth" : 1.02 * mm, "offsetDistance" : 25.4 * mm});
        }
        {
            var Q0;
            Q0=makeQuery(id+"F2.imprint","IMPRINT",FACE,{"disambiguationData":[TD([[makeQuery(id+"F2.imprint","IMPRINT",EDGE,{"derivedFrom":sQuery(id+"F2.wireOp",EDGE,"E11.0")}),-1.0]])]});
            extrude(context, id + "F6", {"entities" : qUnion([Q0]), "operationType" : NewBodyOperationType.REMOVE, "oppositeDirection" : true, "depth" : 3.17 * mm, "offsetDistance" : 25.4 * mm});
        }
        {
            var Q0;
            Q0=makeQuery(id+"F1.opExtrude","CAP_FACE",FACE,{"disambiguationData":[OSD([sQuery(id+"F0.wireOp",EDGE,"E0"),sQuery(id+"F0.wireOp",EDGE,"E1"),sQuery(id+"F0.wireOp",EDGE,"E2"),sQuery(id+"F0.wireOp",EDGE,"E3"),sQuery(id+"F0.wireOp",EDGE,"E4"),sQuery(id+"F0.wireOp",EDGE,"E5")])],"isStart":true});
            var sketch = newSketch(context, id + "F7", { "sketchPlane" : qUnion([Q0])});
            skCircle(sketch, "E20", {"center": v(0, -6.35) * mm, "radius": 2.67 * mm});
            skSolve(sketch);
        }
        {
            var Q0;
            Q0=makeQuery(id+"F7.imprint","IMPRINT",FACE,{"disambiguationData":[TD([[makeQuery(id+"F7.imprint","IMPRINT",EDGE,{"derivedFrom":sQuery(id+"F7.wireOp",EDGE,"E20")}),1.0]])]});
            extrude(context, id + "F8", {"entities" : qUnion([Q0]), "operationType" : NewBodyOperationType.REMOVE, "oppositeDirection" : true, "depth" : 3.8 * mm, "offsetDistance" : 25.4 * mm});
        }
    });
